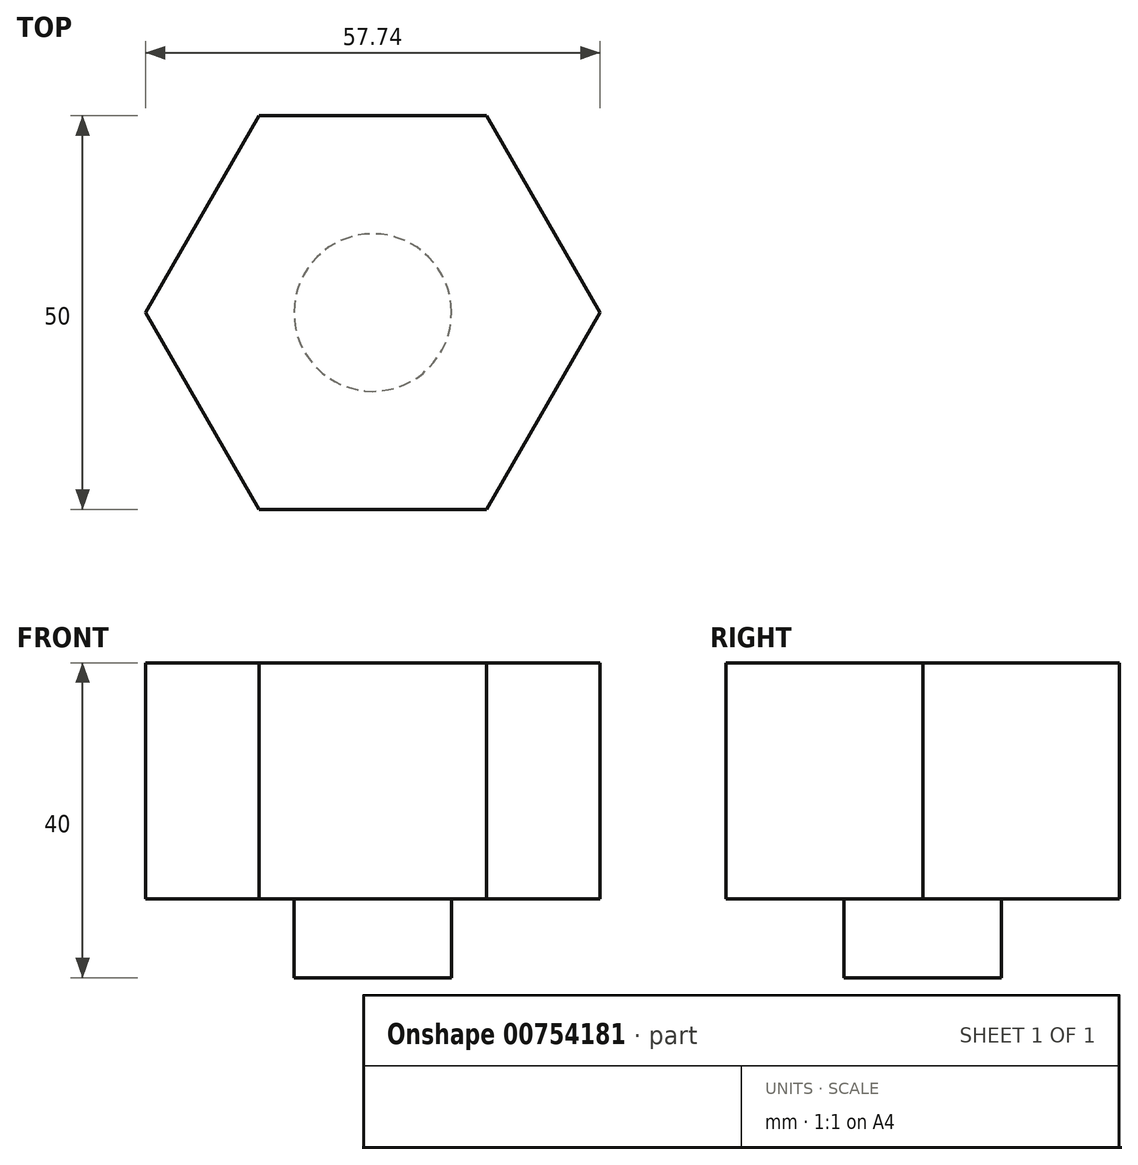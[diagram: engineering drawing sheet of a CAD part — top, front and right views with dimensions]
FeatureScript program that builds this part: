
annotation { "Feature Type Name" : "Feature", "Feature Type Description" : "" }
export const myFeature = defineFeature(function(context is Context, id is Id, definition is map)
    precondition{}
    {
        {
            var Q0;
            Q0=qCreatedBy(makeId("Top.planeOp"),FACE);
            var sketch = newSketch(context, id + "F0", { "sketchPlane" : qUnion([Q0])});
            skCircle(sketch, "E0.cCircle", {"center": v(0, 0) * mm, "radius": 28.87 * mm, "construction": true});
            skLineSegment(sketch, "E0.0", {"start": v(-14.43, 25) * mm, "end": v(14.43, 25) * mm});
            skLineSegment(sketch, "E0.1", {"start": v(14.43, 25) * mm, "end": v(28.87, 0) * mm});
            skLineSegment(sketch, "E0.2", {"start": v(28.87, 0) * mm, "end": v(14.43, -25) * mm});
            skLineSegment(sketch, "E0.3", {"start": v(14.43, -25) * mm, "end": v(-14.43, -25) * mm});
            skLineSegment(sketch, "E0.4", {"start": v(-14.43, -25) * mm, "end": v(-28.87, 0) * mm});
            skLineSegment(sketch, "E0.5", {"start": v(-28.87, 0) * mm, "end": v(-14.43, 25) * mm});
            skSolve(sketch);
        }
        {
            var Q0;
            Q0 = qSketchRegion(id + "F0", true);
            extrude(context, id + "F1", {"entities" : qUnion([Q0]), "depth" : 30 * mm, "offsetDistance" : 25 * mm});
        }
        {
            var Q0;
            Q0=makeQuery(id+"F1.opExtrude","CAP_FACE",FACE,{"disambiguationData":[OSD([sQuery(id+"F0.wireOp",EDGE,"E0.0"),sQuery(id+"F0.wireOp",EDGE,"E0.1"),sQuery(id+"F0.wireOp",EDGE,"E0.2"),sQuery(id+"F0.wireOp",EDGE,"E0.3"),sQuery(id+"F0.wireOp",EDGE,"E0.4"),sQuery(id+"F0.wireOp",EDGE,"E0.5")])],"isStart":true});
            var sketch = newSketch(context, id + "F2", { "sketchPlane" : qUnion([Q0])});
            skCircle(sketch, "E1", {"center": v(0, 0) * mm, "radius": 10 * mm});
            skSolve(sketch);
        }
        {
            var Q0;
            Q0 = qSketchRegion(id + "F2", true);
            extrude(context, id + "F3", {"entities" : qUnion([Q0]), "operationType" : NewBodyOperationType.ADD, "depth" : 10 * mm, "offsetDistance" : 25 * mm});
        }
    });
